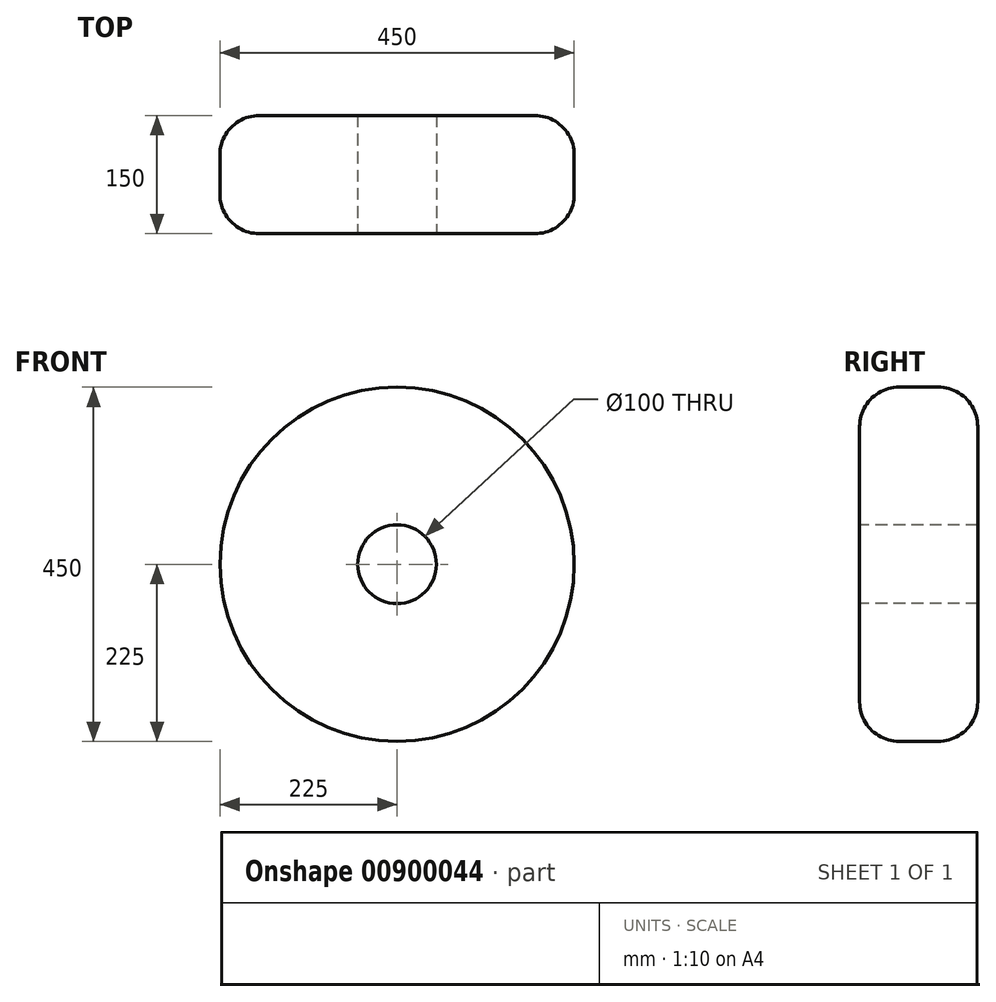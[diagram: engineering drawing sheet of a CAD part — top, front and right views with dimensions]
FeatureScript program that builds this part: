
annotation { "Feature Type Name" : "Feature", "Feature Type Description" : "" }
export const myFeature = defineFeature(function(context is Context, id is Id, definition is map)
    precondition{}
    {
        {
            var Q0;
            Q0=qCreatedBy(makeId("Front.planeOp"),FACE);
            var sketch = newSketch(context, id + "F0", { "sketchPlane" : qUnion([Q0])});
            skCircle(sketch, "E0", {"center": v(0, 0) * mm, "radius": 225 * mm});
            skSolve(sketch);
        }
        {
            var Q0;
            Q0=makeQuery(id+"F0.imprint","IMPRINT",FACE,{"disambiguationData":[TD([[makeQuery(id+"F0.imprint","IMPRINT",EDGE,{"derivedFrom":sQuery(id+"F0.wireOp",EDGE,"E0")}),1.0]])]});
            extrude(context, id + "F1", {"entities" : qUnion([Q0]), "depth" : 150 * mm, "offsetDistance" : 25 * mm});
        }
        {
            var Q0;
            Q0=makeQuery(id+"F1.opExtrude","CAP_EDGE",EDGE,{"disambiguationData":[OSD([sQuery(id+"F0.wireOp",EDGE,"E0")])],"isStart":false});
            var Q1;
            Q1=makeQuery(id+"F1.opExtrude","CAP_EDGE",EDGE,{"disambiguationData":[OSD([sQuery(id+"F0.wireOp",EDGE,"E0")])],"isStart":true});
            fillet(context, id + "F2", {"entities" : qUnion([Q0, Q1]), "radius" : 50 * mm, "tangentPropagation" : true, "allowEdgeOverflow" : false});
        }
        {
            var Q0;
            Q0=makeQuery(id+"F1.opExtrude","CAP_FACE",FACE,{"disambiguationData":[OSD([sQuery(id+"F0.wireOp",EDGE,"E0")])],"isStart":false});
            var sketch = newSketch(context, id + "F3", { "sketchPlane" : qUnion([Q0])});
            skCircle(sketch, "E1", {"center": v(0, 0) * mm, "radius": 50 * mm});
            skSolve(sketch);
        }
        {
            var Q0;
            Q0=sQuery(id+"F3.wireOp",VERTEX,"E1.center");
            var Q1;
            Q1=makeQuery(id+"F1.opExtrude","SWEPT_BODY",BODY,{"disambiguationData":[OSD([sQuery(id+"F0.wireOp",EDGE,"E0")])]});
            hole(context, id + "F4", {"style" : HoleStyle.SIMPLE, "endStyle" : HoleEndStyle.THROUGH, "holeDiameter" : 100 * mm, "majorDiameter" : 5 * mm, "isTappedThrough" : true, "tappedDepth" : 12 * mm, "tapClearance" : 3, "locations" : qUnion([Q0]), "scope" : qUnion([Q1])});
        }
    });
